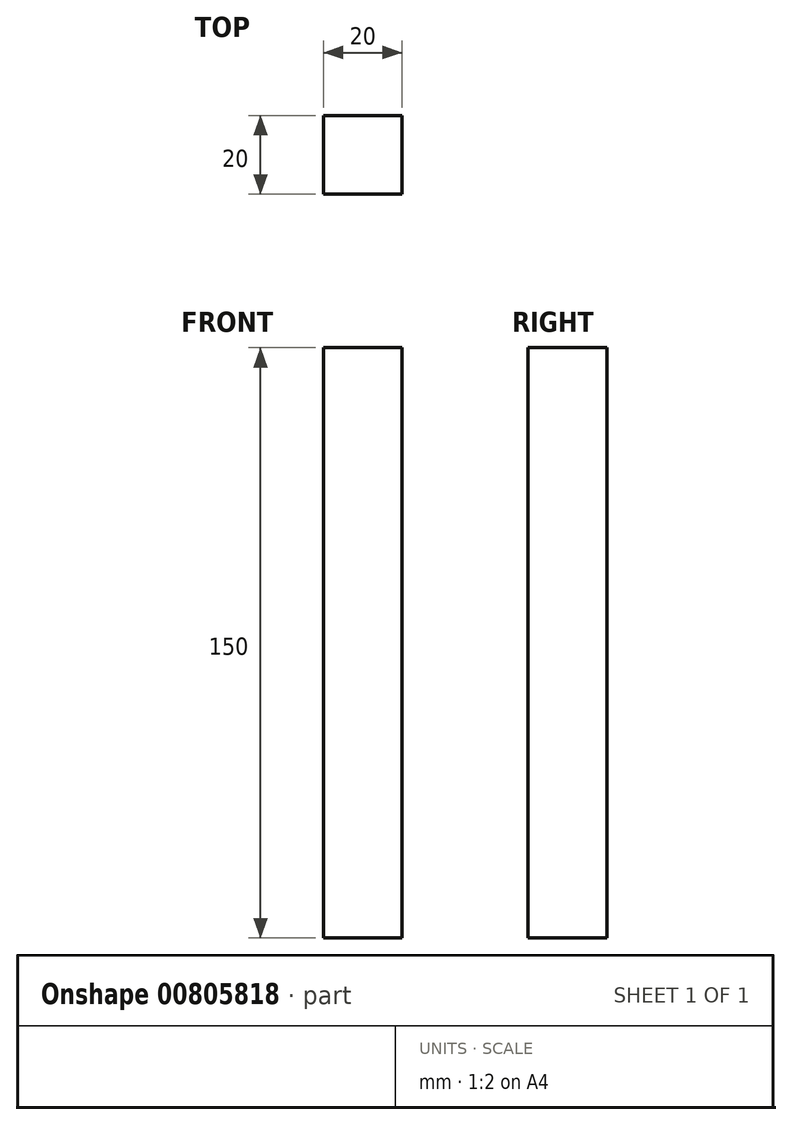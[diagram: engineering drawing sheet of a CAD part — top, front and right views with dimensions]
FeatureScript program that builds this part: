
annotation { "Feature Type Name" : "Feature", "Feature Type Description" : "" }
export const myFeature = defineFeature(function(context is Context, id is Id, definition is map)
    precondition{}
    {
        {
            var Q0;
            Q0=qCreatedBy(makeId("Top.planeOp"),FACE);
            var sketch = newSketch(context, id + "F0", { "sketchPlane" : qUnion([Q0])});
            skLineSegment(sketch, "E0.bottom", {"start": v(-10, 10) * mm, "end": v(10, 10) * mm});
            skLineSegment(sketch, "E0.top", {"start": v(-10, -10) * mm, "end": v(10, -10) * mm});
            skLineSegment(sketch, "E0.left", {"start": v(-10, 10) * mm, "end": v(-10, -10) * mm});
            skLineSegment(sketch, "E0.right", {"start": v(10, 10) * mm, "end": v(10, -10) * mm});
            skSolve(sketch);
        }
        {
            var Q0;
            Q0 = qSketchRegion(id + "F0", true);
            extrude(context, id + "F1", {"entities" : qUnion([Q0]), "depth" : 150 * mm, "offsetDistance" : 25 * mm});
        }
    });
